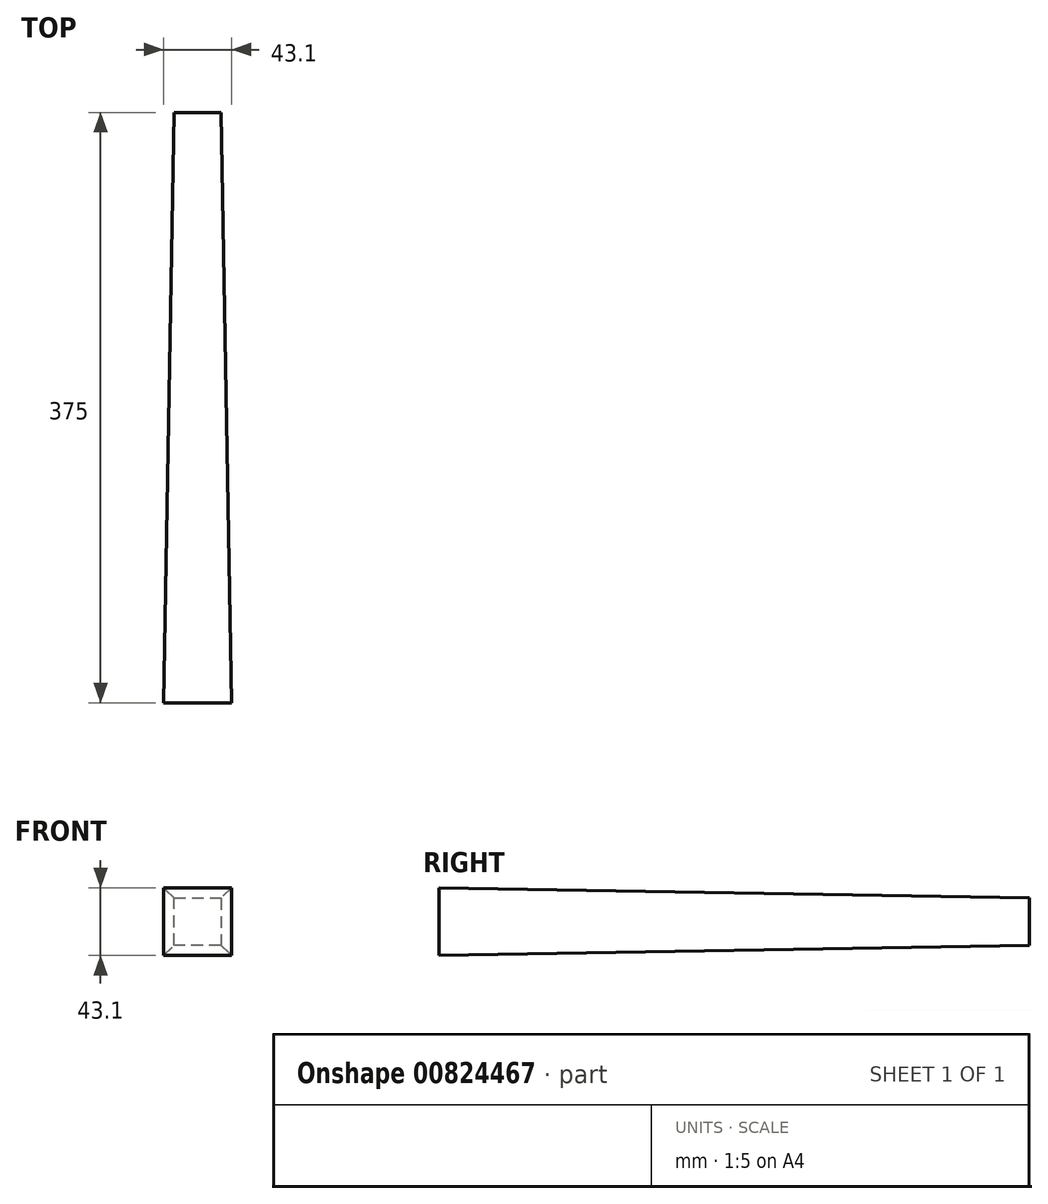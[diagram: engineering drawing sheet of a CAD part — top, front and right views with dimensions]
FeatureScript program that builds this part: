
annotation { "Feature Type Name" : "Feature", "Feature Type Description" : "" }
export const myFeature = defineFeature(function(context is Context, id is Id, definition is map)
    precondition{}
    {
        {
            var Q0;
            Q0=qCreatedBy(makeId("Front.planeOp"),FACE);
            var sketch = newSketch(context, id + "F0", { "sketchPlane" : qUnion([Q0])});
            skLineSegment(sketch, "E0.bottom", {"start": v(0, 0) * mm, "end": v(30, 0) * mm});
            skLineSegment(sketch, "E0.top", {"start": v(0, -30) * mm, "end": v(30, -30) * mm});
            skLineSegment(sketch, "E0.left", {"start": v(0, 0) * mm, "end": v(0, -30) * mm});
            skLineSegment(sketch, "E0.right", {"start": v(30, 0) * mm, "end": v(30, -30) * mm});
            skSolve(sketch);
        }
        {
            var Q0;
            Q0 = qSketchRegion(id + "F0", true);
            extrude(context, id + "F1", {"entities" : qUnion([Q0]), "depth" : 375 * mm, "offsetDistance" : 25 * mm, "hasDraft" : true, "draftAngle" : 1 * degree});
        }
    });
